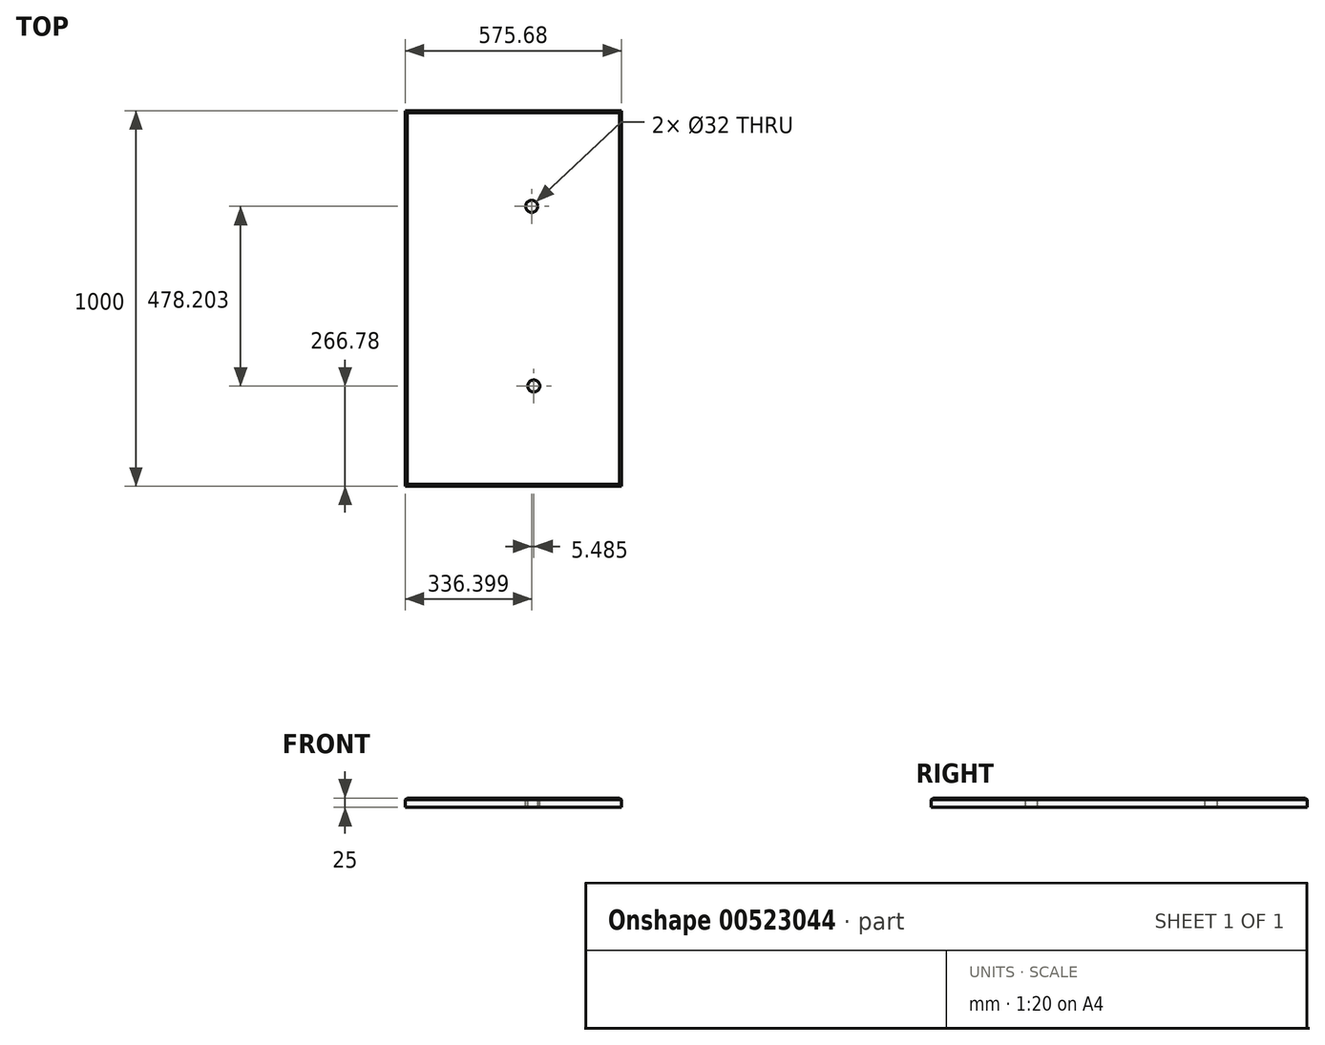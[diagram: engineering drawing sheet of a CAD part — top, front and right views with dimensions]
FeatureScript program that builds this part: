
annotation { "Feature Type Name" : "Feature", "Feature Type Description" : "" }
export const myFeature = defineFeature(function(context is Context, id is Id, definition is map)
    precondition{}
    {
        {
            var Q0;
            Q0=qCreatedBy(makeId("Top.planeOp"),FACE);
            var sketch = newSketch(context, id + "F0", { "sketchPlane" : qUnion([Q0])});
            skLineSegment(sketch, "E0.bottom", {"start": v(-271.42, -127.03) * mm, "end": v(304.26, -127.03) * mm});
            skLineSegment(sketch, "E0.top", {"start": v(-271.42, 872.97) * mm, "end": v(304.26, 872.97) * mm});
            skLineSegment(sketch, "E0.left", {"start": v(-271.42, -127.03) * mm, "end": v(-271.42, 872.97) * mm});
            skLineSegment(sketch, "E0.right", {"start": v(304.26, -127.03) * mm, "end": v(304.26, 872.97) * mm});
            skSolve(sketch);
        }
        {
            var Q0;
            Q0=makeQuery(id+"F0.imprint","IMPRINT",FACE,{"disambiguationData":[TD([[makeQuery(id+"F0.imprint","IMPRINT",EDGE,{"derivedFrom":sQuery(id+"F0.wireOp",EDGE,"E0.bottom")}),1.0]])]});
            extrude(context, id + "F1", {"entities" : qUnion([Q0]), "depth" : 25 * mm, "offsetDistance" : 25 * mm});
        }
        {
            var Q0;
            Q0=makeQuery(id+"F1.opExtrude","CAP_FACE",FACE,{"disambiguationData":[OSD([sQuery(id+"F0.wireOp",EDGE,"E0.bottom"),sQuery(id+"F0.wireOp",EDGE,"E0.top"),sQuery(id+"F0.wireOp",EDGE,"E0.left"),sQuery(id+"F0.wireOp",EDGE,"E0.right")])],"isStart":false});
            var sketch = newSketch(context, id + "F2", { "sketchPlane" : qUnion([Q0])});
            skSolve(sketch);
        }
        {
            var Q0;
            Q0=makeQuery(id+"F1.opExtrude","CAP_EDGE",EDGE,{"disambiguationData":[OSD([sQuery(id+"F0.wireOp",EDGE,"E0.bottom")])],"isStart":false});
            chamfer(context, id + "F3", {"entities" : qUnion([Q0]), "width" : 5 * mm, "tangentPropagation" : true});
        }
        {
            var Q0;
            Q0=makeQuery(id+"F1.opExtrude","CAP_EDGE",EDGE,{"disambiguationData":[OSD([sQuery(id+"F0.wireOp",EDGE,"E0.right")])],"isStart":false});
            chamfer(context, id + "F4", {"entities" : qUnion([Q0]), "width" : 5 * mm, "tangentPropagation" : true});
        }
        {
            var Q0;
            Q0=makeQuery(id+"F1.opExtrude","CAP_EDGE",EDGE,{"disambiguationData":[OSD([sQuery(id+"F0.wireOp",EDGE,"E0.left")])],"isStart":false});
            chamfer(context, id + "F5", {"entities" : qUnion([Q0]), "width" : 5 * mm, "tangentPropagation" : true});
        }
        {
            var Q0;
            Q0=makeQuery(id+"F1.opExtrude","CAP_EDGE",EDGE,{"disambiguationData":[OSD([sQuery(id+"F0.wireOp",EDGE,"E0.top")])],"isStart":false});
            chamfer(context, id + "F6", {"entities" : qUnion([Q0]), "width" : 5 * mm, "tangentPropagation" : true});
        }
        {
            var Q0;
            Q0=makeQuery(id+"F2.imprint","IMPRINT",FACE,{"disambiguationData":[TD([[makeQuery(id+"F2.imprint","IMPRINT",EDGE,{"derivedFrom":makeQuery(id+"F1.opExtrude","CAP_EDGE",EDGE,{"disambiguationData":[OSD([sQuery(id+"F0.wireOp",EDGE,"E0.bottom")])],"isStart":false})}),1.0]])]});
            var sketch = newSketch(context, id + "F7", { "sketchPlane" : qUnion([Q0])});
            skPoint(sketch, "E1", {"position": v(64.98, 617.95) * mm});
            skPoint(sketch, "E2", {"position": v(70.46, 139.75) * mm});
            skSolve(sketch);
        }
        {
            var Q0;
            Q0=sQuery(id+"F7.wireOp",VERTEX,"E1");
            var Q1;
            Q1=sQuery(id+"F7.wireOp",VERTEX,"E2");
            var Q2;
            Q2=makeQuery(id+"F1.opExtrude","SWEPT_BODY",BODY,{"disambiguationData":[OSD([sQuery(id+"F0.wireOp",EDGE,"E0.bottom"),sQuery(id+"F0.wireOp",EDGE,"E0.top"),sQuery(id+"F0.wireOp",EDGE,"E0.left"),sQuery(id+"F0.wireOp",EDGE,"E0.right")])]});
            hole(context, id + "F8", {"style" : HoleStyle.SIMPLE, "endStyle" : HoleEndStyle.THROUGH, "holeDiameter" : 32 * mm, "isTappedThrough" : true, "tappedDepth" : 12 * mm, "tapClearance" : 3, "startFromSketch" : true, "locations" : qUnion([Q0, Q1]), "scope" : qUnion([Q2])});
        }
    });
